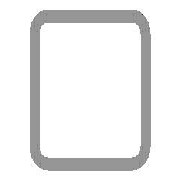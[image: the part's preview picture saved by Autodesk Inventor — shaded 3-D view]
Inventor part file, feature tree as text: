
AUTODESK INVENTOR PART (.ipt)
format: ipt  version: 2025.3 (Build 293356030, 356C)  size: 150,528 bytes
history: native  units: mm (DEFAULTED — no unit token found)
features: other x4, plane x3, split x2, sketch x1
ambient origin geometry x8: Origin, YZ Plane, XZ Plane, XY Plane, X Axis, Y Axis, Z Axis, Center Point
bodies: Solid1 (feature_tree), Body (feature_tree)
feature tree (10):
  parser-record x1  (decoder bookkeeping rows leaked as tree rows — omitted from the tree; the rows remain in map.json)
  other  "Driven Length"
  other  "Start Plane"
  other  "End Plane"
  plane  "Work Plane4"
  split  "Split1"
  plane  "Work Plane5"
  split  "Split2"
  sketch  "Sketch3"  dims[d3=826.981276mm d4=0.0mm d7=4.0mm d9=40.0mm d11=40.0mm d12=2.0mm d13=71.810467mm d14=898.791742mm d15=20.0mm d16=20.0mm d17=90.0deg d18=826.981276mm]
  plane  "Work Plane3"
